# Revit family: ElectricalEquipment_Hager_TPNLighting&Power_HagerTPNExtBoxCable(nodoor)
name_source: partatom
category: Electrical Equipment
revit_build: Autodesk Revit 2015 (Build: 20160512_1515(x64)
units: mm (PartAtom-declared; Revit-internal decimal feet)

## types (24) — shared parameters
CE Approval = Yes
Colour = BS4800:2011 00A01 Oyster Grey
Default Elevation = 1200 mm
Design Country = China
Enclosure Rating = IP3X
Frequency = 50 Hz
Location = Indoors
Location of Manufacturer = Telford, TF1 7FT
MCB Rating = 0 A
Manufacturer = Hager UK Ltd
Manufacturer Country = United Kingdom
Manufacturer Website = www.hager.co.uk
Neutral Rating = 0.00%
Packaging Recyclable = Yes
Packaging Weight = 0.50 kg
Pollution Degree = 2
Product Family = TPN JK1 Ext Box Cable
Product Group = TPN
Reference Standard = BS EN 62208
Revision = 2
Shape = Rectangular
Supply Phase = 1
Type = ElectricalFixture
URL = www.hager.co.uk
Ui Rating = 690 V
Voltage = 230
Warranty ID = 24 Months
zero-valued in all types: Door

## per-type parameters (varying)
| type | Description | EAN | Hager Catalogue Ref | Model | Overall Height | Overall Width | Product Description | Product Literature | Product Range | Product Weight | Type Comments |
| TPN JK1 Ext Box Cable Side Full Width (04W) | Invicta 3 TPN JK1 Side Cable Extension (4W) | 5015652251514 | JK104BSF | JK104BSF | 92 mm  [stored 0.301837 ft] | 465 mm  [stored 1.52559 ft] | Invicta 3 TPN JK1 Side Cable Extension (4W) | www.hager.co.uk/?artnr=JK104BSF | Invicta 3 TPN JK1 Cable Extension (4W) | 8.00 kg | Mounted on LHS or RHS of DB or free standing |
| TPN JK1 Ext Box Cable Side Full Width (06W) | Invicta 3 TPN JK1 Side Cable Extension (6W) | 5015652251583 | JK106BSF | JK106BSF | 92 mm  [stored 0.301837 ft] | 465 mm  [stored 1.52559 ft] | Invicta 3 TPN JK1 Side Cable Extension (6W) | www.hager.co.uk/?artnr=JK106BSF | Invicta 3 TPN JK1 Cable Extension (6W) | 8.50 kg | Mounted on LHS or RHS of DB or free standing |
| TPN JK1 Ext Box Cable Side Full Width (08W) | Invicta 3 TPN JK1 Side Cable Extension (8W) | 5015652251651 | JK108BSF | JK108BSF | 92 mm  [stored 0.301837 ft] | 465 mm  [stored 1.52559 ft] | Invicta 3 TPN JK1 Side Cable Extension (8W) | www.hager.co.uk/?artnr=JK108BSF | Invicta 3 TPN JK1 Cable Extension (8W) | 9.00 kg | Mounted on LHS or RHS of DB or free standing |
| TPN JK1 Ext Box Cable Side Full Width (12W) | Invicta 3 TPN JK1 Side Cable Extension (12W) | 5015652251781 | JK112BSF | JK112BSF | 92 mm  [stored 0.301837 ft] | 465 mm  [stored 1.52559 ft] | Invicta 3 TPN JK1 Side Cable Extension (12W) | www.hager.co.uk/?artnr=JK112BSF | Invicta 3 TPN JK1 Cable Extension (12W) | 10.50 kg | Mounted on LHS or RHS of DB or free standing |
| TPN JK1 Ext Box Cable Side Full Width (16W) | Invicta 3 TPN JK1 Side Cable Extension (16W) | 5015652251842 | JK116BSF | JK116BSF | 92 mm  [stored 0.301837 ft] | 465 mm  [stored 1.52559 ft] | Invicta 3 TPN JK1 Side Cable Extension (16W) | www.hager.co.uk/?artnr=JK116BSF | Invicta 3 TPN JK1 Cable Extension (16W) | 12.00 kg | Mounted on LHS or RHS of DB or free standing |
| TPN JK2 Ext Box Cable Side Full Width (08W) | Invicta 3 TPN JK2 Side Cable Extension (8W) | 5015652252092 | JK208BSF | JK208BSF | 125 mm  [stored 0.410105 ft] | 465 mm  [stored 1.52559 ft] | Invicta 3 TPN JK2 Side Cable Extension (8W) | www.hager.co.uk/?artnr=JK208BSF | Invicta 3 TPN JK2 Cable Extension (8W) | 10.00 kg | Mounted on LHS or RHS of DB or free standing |
| TPN JK2 Ext Box Cable Side Full Width (12W) | Invicta 3 TPN JK2 Side Cable Extension (12W) | 5015652252153 | JK212BSF | JK212BSF | 125 mm  [stored 0.410105 ft] | 465 mm  [stored 1.52559 ft] | Invicta 3 TPN JK2 Side Cable Extension (12W) | www.hager.co.uk/?artnr=JK212BSF | Invicta 3 TPN JK2 Cable Extension (12W) | 11.00 kg | Mounted on LHS or RHS of DB or free standing |
| TPN JK2 Ext Box Cable Side Full Width (16W) | Invicta 3 TPN JK2 Side Cable Extension (16W) | 5015652252214 | JK216BSF | JK216BSF | 125 mm  [stored 0.410105 ft] | 465 mm  [stored 1.52559 ft] | Invicta 3 TPN JK2 Side Cable Extension (16W) | www.hager.co.uk/?artnr=JK216BSF | Invicta 3 TPN JK2 Cable Extension (16W) | 12.50 kg | Mounted on LHS or RHS of DB or free standing |
| TPN JK2 Ext Box Cable Side Full Width (18W) | Invicta 3 TPN JK2 Side Cable Extension (18W) | 5015652252252 | JK218BSF | JK218BSF | 125 mm  [stored 0.410105 ft] | 465 mm  [stored 1.52559 ft] | Invicta 3 TPN JK2 Side Cable Extension (18W) | www.hager.co.uk/?artnr=JK218BSF | Invicta 3 TPN JK2 Cable Extension (18W) | 13.00 kg | Mounted on LHS or RHS of DB or free standing |
| TPN JK2 Ext Box Cable Side Full Width (24W) | Invicta 3 TPN JK2 Side Cable Extension (24W) | 5015652252320 | JK224BSF | JK224BSF | 125 mm  [stored 0.410105 ft] | 465 mm  [stored 1.52559 ft] | Invicta 3 TPN JK2 Side Cable Extension (24W) | www.hager.co.uk/?artnr=JK224BSF | Invicta 3 TPN JK2 Cable Extension (24W) | 15.00 kg | Mounted on LHS or RHS of DB or free standing |
| TPN JK1 Ext Box Cable Side Half Width (04W) | Invicta 3 TPN JK1 Side Cable Extension (4W) | 5015652251538 | JK104BSH | JK104BSH | 92 mm  [stored 0.301837 ft] | 233 mm  [stored 0.764436 ft] | Invicta 3 TPN JK1 Side Cable Extension (4W) | www.hager.co.uk/?artnr=JK104BSH | Invicta 3 TPN JK1 Cable Extension (4W) | 6.50 kg | Mounted on LHS or RHS of DB or free standing |
| TPN JK1 Ext Box Cable Side Half Width (06W) | Invicta 3 TPN JK1 Side Cable Extension (6W) | 5015652251606 | JK106BSH | JK106BSH | 92 mm  [stored 0.301837 ft] | 233 mm  [stored 0.764436 ft] | Invicta 3 TPN JK1 Side Cable Extension (6W) | www.hager.co.uk/?artnr=JK106BSH | Invicta 3 TPN JK1 Cable Extension (6W) | 7.50 kg | Mounted on LHS or RHS of DB or free standing |
| TPN JK1 Ext Box Cable Side Half Width (08W) | Invicta 3 TPN JK1 Side Cable Extension (8W) | 5015652251675 | JK108BSH | JK108BSH | 92 mm  [stored 0.301837 ft] | 233 mm  [stored 0.764436 ft] | Invicta 3 TPN JK1 Side Cable Extension (8W) | www.hager.co.uk/?artnr=JK108BSH | Invicta 3 TPN JK1 Cable Extension (8W) | 8.00 kg | Mounted on LHS or RHS of DB or free standing |
| TPN JK1 Ext Box Cable Side Half Width (12W) | Invicta 3 TPN JK1 Side Cable Extension (12W) | 5015652251804 | JK112BSH | JK112BSH | 92 mm  [stored 0.301837 ft] | 233 mm  [stored 0.764436 ft] | Invicta 3 TPN JK1 Side Cable Extension (12W) | www.hager.co.uk/?artnr=JK112BSH | Invicta 3 TPN JK1 Cable Extension (12W) | 9.50 kg | Mounted on LHS or RHS of DB or free standing |
| TPN JK1 Ext Box Cable Side Half Width (16W) | Invicta 3 TPN JK1 Side Cable Extension (16W) | 5015652251866 | JK116BSH | JK116BSH | 92 mm  [stored 0.301837 ft] | 233 mm  [stored 0.764436 ft] | Invicta 3 TPN JK1 Side Cable Extension (16W) | www.hager.co.uk/?artnr=JK116BSH | Invicta 3 TPN JK1 Cable Extension (16W) | 10.50 kg | Mounted on LHS or RHS of DB or free standing |
| TPN JK2 Ext Box Cable Side Half Width (08W) | Invicta 3 TPN JK2 Side Cable Extension (8W) | 50156522515145015652252115
5015652252115
5015652252115 | JK208BSH | JK208BSH | 125 mm  [stored 0.410105 ft] | 233 mm  [stored 0.764436 ft] | Invicta 3 TPN JK2 Side Cable Extension (8W) | www.hager.co.uk/?artnr=JK208BSH | Invicta 3 TPN JK2 Cable Extension (8W) | 10.00 kg | Mounted on LHS or RHS of DB or free standing |
| TPN JK2 Ext Box Cable Side Half Width (12W) | Invicta 3 TPN JK2 Side Cable Extension (12W) | 5015652252177 | JK212BSH | JK212BSH | 125 mm  [stored 0.410105 ft] | 233 mm  [stored 0.764436 ft] | Invicta 3 TPN JK2 Side Cable Extension (12W) | www.hager.co.uk/?artnr=JK212BSH | Invicta 3 TPN JK2 Cable Extension (12W) | 11.00 kg | Mounted on LHS or RHS of DB or free standing |
| TPN JK2 Ext Box Cable Side Half Width (16W) | Invicta 3 TPN JK2 Side Cable Extension (16W) | 5015652252238 | JK216BSH | JK216BSH | 125 mm  [stored 0.410105 ft] | 233 mm  [stored 0.764436 ft] | Invicta 3 TPN JK2 Side Cable Extension (16W) | www.hager.co.uk/?artnr=JK216BSH | Invicta 3 TPN JK2 Cable Extension (16W) | 12.50 kg | Mounted on LHS or RHS of DB or free standing |
| TPN JK2 Ext Box Cable Side Half Width (18W) | Invicta 3 TPN JK2 Side Cable Extension (18W) | 5015652252276 | JK218BSH | JK218BSH | 125 mm  [stored 0.410105 ft] | 233 mm  [stored 0.764436 ft] | Invicta 3 TPN JK2 Side Cable Extension (18W) | www.hager.co.uk/?artnr=JK218BSH | Invicta 3 TPN JK2 Cable Extension (18W) | 13.00 kg | Mounted on LHS or RHS of DB or free standing |
| TPN JK2 Ext Box Cable Side Half Width (24W) | Invicta 3 TPN JK2 Side Cable Extension (24W) | 5015652252344 | JK224BSH | JK224BSH | 125 mm  [stored 0.410105 ft] | 233 mm  [stored 0.764436 ft] | Invicta 3 TPN JK2 Side Cable Extension (24W) | www.hager.co.uk/?artnr=JK224BSH | Invicta 3 TPN JK2 Cable Extension (24W) | 15.00 kg | Mounted on LHS or RHS of DB or free standing |
| TPN JK1 Ext Box Cable Side (Small) | Invicta 3 TPN JK1 Cable Extension (Small) | 5015654758172 | JK101SE | JK101SE | 92 mm  [stored 0.301837 ft] | 465 mm  [stored 1.52559 ft] | Invicta 3 TPN JK1 Cable Extension (Small) | www.hager.co.uk/?artnr=JK101SE | Invicta 3 TPN JK1 Cable Extension (Small) | 3.50 kg | Mounted above or below DB |
| TPN JK1 Ext Box Cable Side (Large) | Invicta 3 TPN JK1 Cable Extension (Large) | 5015652251477 | JK102LE | JK102LE | 92 mm  [stored 0.301837 ft] | 465 mm  [stored 1.52559 ft] | Invicta 3 TPN JK1 Cable Extension (Large) | www.hager.co.uk/?artnr=JK102LE | Invicta 3 TPN JK1 Cable Extension (Large) | 4.80 kg | Mounted above or below DB |
| TPN JK2 Ext Box Cable Side (Small) | Invicta 3 TPN JK2 Cable Extension (Small) | 5015652252023 | JK201SE | JK201SE | 125 mm  [stored 0.410105 ft] | 465 mm  [stored 1.52559 ft] | Invicta 3 TPN JK2 Cable Extension (Small) | www.hager.co.uk/?artnr=JK201SE | Invicta 3 TPN JK2 Cable Extension (Small) | 6.00 kg | Mounted above or below DB |
| TPN JK2 Ext Box Cable Side (Large) | Invicta 3 TPN JK2 Cable Extension (Large) | 5015652252047 | JK202LE | JK202LE | 125 mm  [stored 0.410105 ft] | 465 mm  [stored 1.52559 ft] | Invicta 3 TPN JK2 Cable Extension (Large) | www.hager.co.uk/?artnr=JK202LE | Invicta 3 TPN JK2 Cable Extension (Large) | 10.00 kg | Mounted above or below DB |

note: [stored X ft] marks values corroborated as IEEE doubles in the binary element streams (Revit-internal decimal feet)

## geometry (parser evidence)
native form markers: Sweep x4
no freeform markers — native parametric forms only
